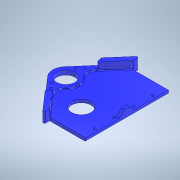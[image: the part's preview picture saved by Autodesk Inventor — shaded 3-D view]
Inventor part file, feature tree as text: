
AUTODESK INVENTOR PART (.ipt)
format: ipt  version: 2022 (Build 260153000, 153)  size: 398,336 bytes
history: native  units: in
note: dims shown in document units (in); Inventor stores cm internally (conversion verified against a paired STEP export)
features: sketch x12, extrude x9, projected_geometry x5, reference x4, other x4, hole x3, fillet x2, chamfer x2, mirror x1
ambient origin geometry x8: Origin, YZ Plane, XZ Plane, XY Plane, X Axis, Y Axis, Z Axis, Center Point
bodies: Solid3 (feature_tree)
feature tree (42):
  extrude  "Extrusion13"  Depth=2.1654in
  extrude  "Extrusion14"  Depth=0.4433in TaperAngle=0.0deg
  mirror  "Mirror4"
  extrude  "Extrusion25"  Depth=0.1969in TaperAngle=0.0deg
  extrude  "Extrusion26"  Depth=1.5748in
  extrude  "Extrusion28"  Depth=0.1969in
  extrude  "Extrusion35"  Depth=0.5906in
  extrude  "Extrusion38"  Depth=1.1811in
  extrude  "Extrusion39"  TaperAngle=0.0deg  [1 undecoded]
  hole  "Hole5"  [1 undecoded]
  fillet  "Fillet3"  [1 undecoded]
  fillet  "Fillet4"  Radius=1.5354in
  hole  "Hole6"  [1 undecoded]
  hole  "Hole7"  [1 undecoded]
  chamfer  "Chamfer3"  Distance=0.3937in
  chamfer  "Chamfer4"  Distance=0.9449in
  extrude  "Extrusion40"  Depth=0.3937in
  sketch  "Sketch14"  dims[d94=0.9646in d95=2.1654in]
  sketch  "Sketch15"  dims[d96=1.7717in d97=0.4433in d98=0.0in]
  projected_geometry  "Projected Loop7"
  sketch  "Sketch26"  dims[d99=2.5561in d100=0.1969in d101=0.0in]
  sketch  "Sketch27"  dims[d137=0.7874in d138=1.5748in]
  sketch  "Sketch29"  dims[d139=0.1969in d140=0.0in d141=1.1024in]
  sketch  "Sketch37"  dims[d143=0.0787in d144=0.0in d145=0.5906in]
  projected_geometry  "Projected Loop19"
  sketch  "Sketch40"  dims[d146=1.1024in d151=1.1811in]
  projected_geometry  "Projected Loop20"
  sketch  "Sketch41"  dims[d152=0.3937in d153=0.0in d185=0.0in d186=0.0in]
  projected_geometry  "Projected Loop21"
  sketch  "Sketch42"  dims[d198=0.4724in d199=0.4724in d200=0.0in d201=0.0in d202=1.5354in]
  projected_geometry  "Projected Loop22"
  sketch  "Sketch43"  dims[d203=1.7717in d204=1.8504in]
  reference  "Reference1"
  reference  "Reference2"
  sketch  "Sketch44"  dims[d205=0.3937in d206=0.0in d207=1.8504in]
  reference  "Reference3"
  reference  "Reference4"
  sketch  "Sketch45"  dims[d208=0.3937in d209=0.3937in d210=0.9449in d211=0.3937in d213=0.3937in d214=0.9055in d215=0.9055in d216=0.1969in d217=0.1969in d220=1.1811in d221=1.1811in d222=1.1811in d223=0.7553in d224=0.7553in d225=1.1811in d226=0.1575in d227=0.2362in d228=0.248in d229=0.0787in d230=90.0deg d231=0.2756in d232=0.0in d233=0.0787in d234=0.0394in d235=0.1575in d236=0.2362in d237=0.1575in d238=0.0787in d239=90.0deg d240=0.315in d241=0.8108in d242=0.1575in d243=0.2362in d244=0.1575in d245=0.0787in d246=90.0deg d247=0.315in d248=0.8108in d249=0.0394in d250=0.0787in d251=45.0deg d252=0.1575in d253=0.0787in d254=45.0deg d255=0.2913in d256=0.315in d257=135.0deg d258=0.1969in d259=0.0in d93=0.1575in d107=0.0197in d108=0.0344in d109=0.0197in d110=0.0344in d154=0.0197in d155=0.0344in]
  parser-record x1  (decoder bookkeeping rows leaked as tree rows — omitted from the tree; the rows remain in map.json)
  other  "Main Body.iam"
  other  "Front Armor:2"
  other  "Front Armor:1"
note: 5 required parameter values undecoded (feature->parameter linkage not recoverable at this tier; creation-order binding heuristic only, values carry confidence <= 0.55)
note: 1 file-system path scrubbed to <path> (originals preserved in map.json)
